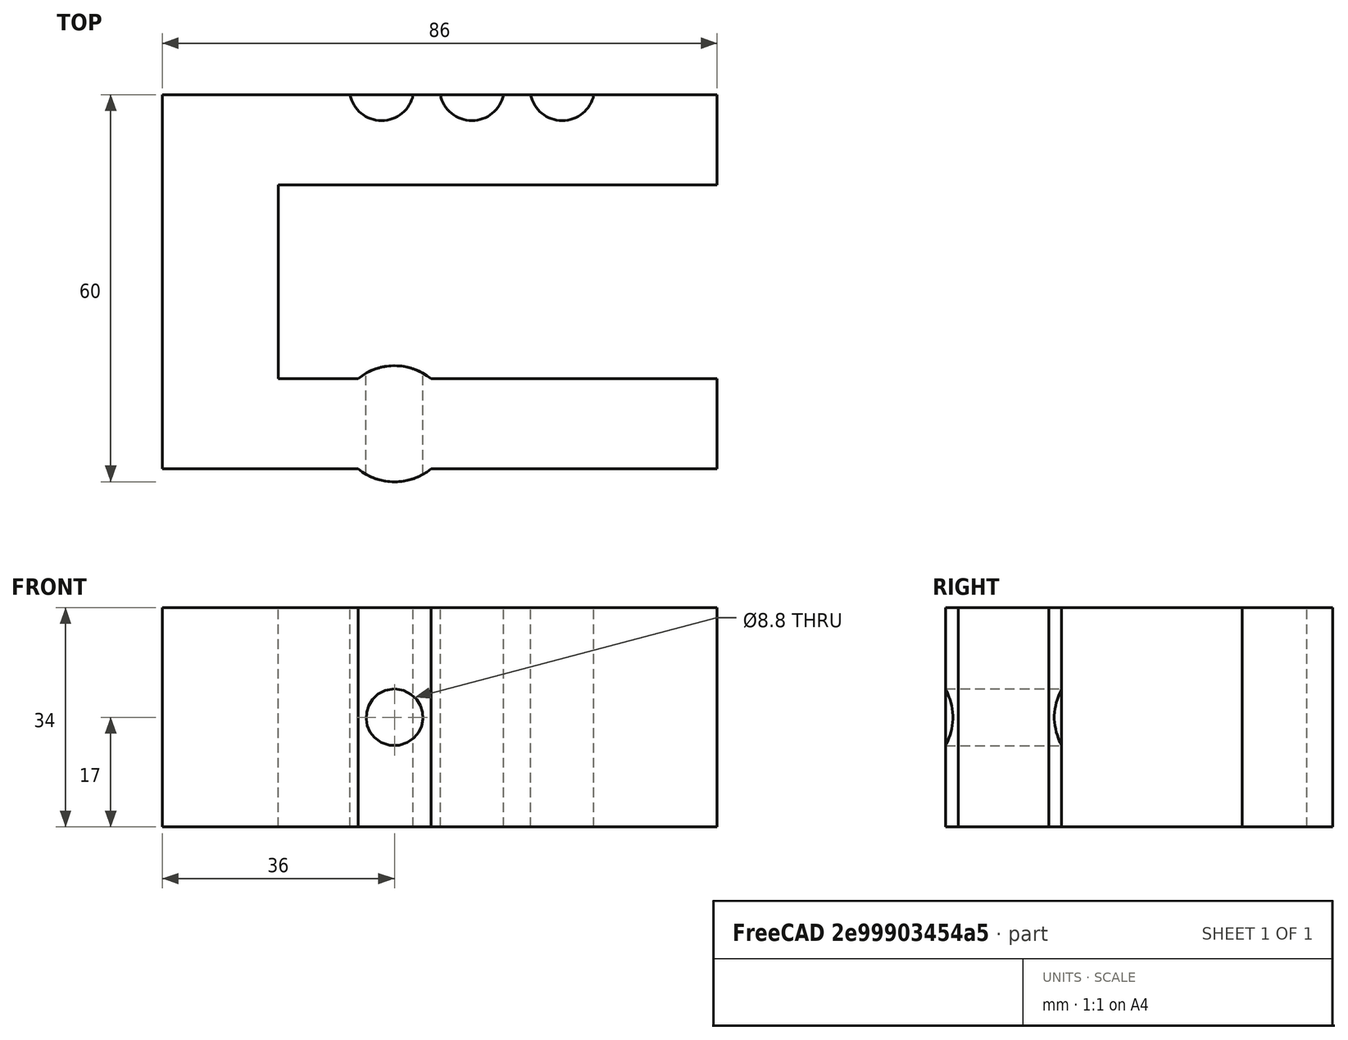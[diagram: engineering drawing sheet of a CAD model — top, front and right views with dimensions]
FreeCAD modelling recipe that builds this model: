
FCSTD DOCUMENT  (FreeCAD 1.2R20251230 (Git shallow))
Label: vanity_cable_clamp_body
License: Creative Commons Attribution 4.0
LicenseURL: https://creativecommons.org/licenses/by/4.0/
objects: Part::Feature×5, Part::Cut×4, Sketcher::SketchObject×2, PartDesign::Pad×2, App::Point×1, PartDesign::Body×1
note: 20 computed .brp shape members not serialized (recipe doc carries the construction recipe); baked Part::Feature solids carry a one-line shape summary decoded from their .brp

FEATURE [App::Point] Origin001
  Role = Origin
FEATURE [Sketcher::SketchObject] Sketch_01_CClamp_Side_Profile
  ArcFitTolerance = 1e-06
  ExternalTypes = [0]
  FullyConstrained = false
  MakeInternals = false
  sketch-geometry (8):
    g0: LineSegment StartX=0 StartY=0 StartZ=0 EndX=86 EndY=0 EndZ=0
    g1: LineSegment StartX=86 StartY=0 StartZ=0 EndX=86 EndY=14 EndZ=0
    g2: LineSegment StartX=86 StartY=14 StartZ=0 EndX=18 EndY=14 EndZ=0
    g3: LineSegment StartX=18 StartY=14 StartZ=0 EndX=18 EndY=44 EndZ=0
    g4: LineSegment StartX=18 StartY=44 StartZ=0 EndX=86 EndY=44 EndZ=0
    g5: LineSegment StartX=86 StartY=44 StartZ=0 EndX=86 EndY=58 EndZ=0
    g6: LineSegment StartX=86 StartY=58 StartZ=0 EndX=0 EndY=58 EndZ=0
    g7: LineSegment StartX=0 StartY=58 StartZ=0 EndX=0 EndY=0 EndZ=0
  constraints (8):
    c: Coincident(g0,g1)
    c: Coincident(g1,g2)
    c: Coincident(g2,g3)
    c: Coincident(g3,g4)
    c: Coincident(g4,g5)
    c: Coincident(g5,g6)
    c: Coincident(g6,g7)
    c: Coincident(g7,g0)
FEATURE [PartDesign::Pad] Pad_02_CClamp_Body
  Direction = (0,0,1)
  Length = 34
  Length2 = 10
  Profile = -> Sketch_01_CClamp_Side_Profile
  Refine = true
  SideType = 0
  Suppressed = false
  Type = 0
  Type2 = 0
FEATURE [Sketcher::SketchObject] Sketch_03_Knob_Hole_Boss
  ArcFitTolerance = 1e-06
  ExternalTypes = [0]
  FullyConstrained = false
  MakeInternals = false
  sketch-geometry (1):
    g0: Circle CenterX=36 CenterY=7 CenterZ=0 NormalX=0 NormalY=0 NormalZ=1 AngleXU=0 Radius=9
  constraints (1):
    c: Radius(g0) = 9
FEATURE [PartDesign::Pad] Pad_04_Knob_Hole_Boss
  BaseFeature = -> Pad_02_CClamp_Body
  Direction = (0,0,1)
  Length = 34
  Length2 = 10
  Profile = -> Sketch_03_Knob_Hole_Boss
  Refine = true
  SideType = 0
  Suppressed = false
  Type = 0
  Type2 = 0
FEATURE [PartDesign::Body] Body_CClampCableGuide
  AllowCompound = true
  Group = -> [Sketch_01_CClamp_Side_Profile,Pad_02_CClamp_Body,Sketch_03_Knob_Hole_Boss,Pad_04_Knob_Hole_Boss]
  Origin = -> Origin
  Tip = -> Pad_04_Knob_Hole_Boss
FEATURE [Part::Feature] _05_Fused_Clamp_And_Boss
  shape: bbox 86 x 60 x 34 mm, 14 faces (baked)
FEATURE [Part::Feature] _06_Tool_Vertical_Knob_Clearance_Hole
  shape: bbox 8.8 x 18 x 8.8 mm, 3 faces (baked)
FEATURE [Part::Cut] _07_Cut_Knob_Clearance_Hole
  Base = -> _05_Fused_Clamp_And_Boss
  Refine = true
  Tool = -> _06_Tool_Vertical_Knob_Clearance_Hole
FEATURE [Part::Feature] _08_Tool_Cable_Channel_1
  Placement = pos=(0,57,-61) rot=(1,0,0;1.5708rad)
  shape: bbox 10 x 10 x 38 mm, 3 faces (baked)
FEATURE [Part::Feature] _08_Tool_Cable_Channel_2
  Placement = pos=(0,57,-61) rot=(1,0,0;1.5708rad)
  shape: bbox 10 x 10 x 38 mm, 3 faces (baked)
FEATURE [Part::Feature] _08_Tool_Cable_Channel_3
  Placement = pos=(0,57,-61) rot=(1,0,0;1.5708rad)
  shape: bbox 10 x 10 x 38 mm, 3 faces (baked)
FEATURE [Part::Cut] _09_Cut_Cable_Channel_1
  Base = -> _07_Cut_Knob_Clearance_Hole
  Refine = true
  Tool = -> _08_Tool_Cable_Channel_1
FEATURE [Part::Cut] _09_Cut_Cable_Channel_2
  Base = -> _09_Cut_Cable_Channel_1
  Refine = true
  Tool = -> _08_Tool_Cable_Channel_2
FEATURE [Part::Cut] _09_Cut_Cable_Channel_3  label="Final_ClampBody_With_CableGuide"
  Base = -> _09_Cut_Cable_Channel_2
  Refine = true
  Tool = -> _08_Tool_Cable_Channel_3
